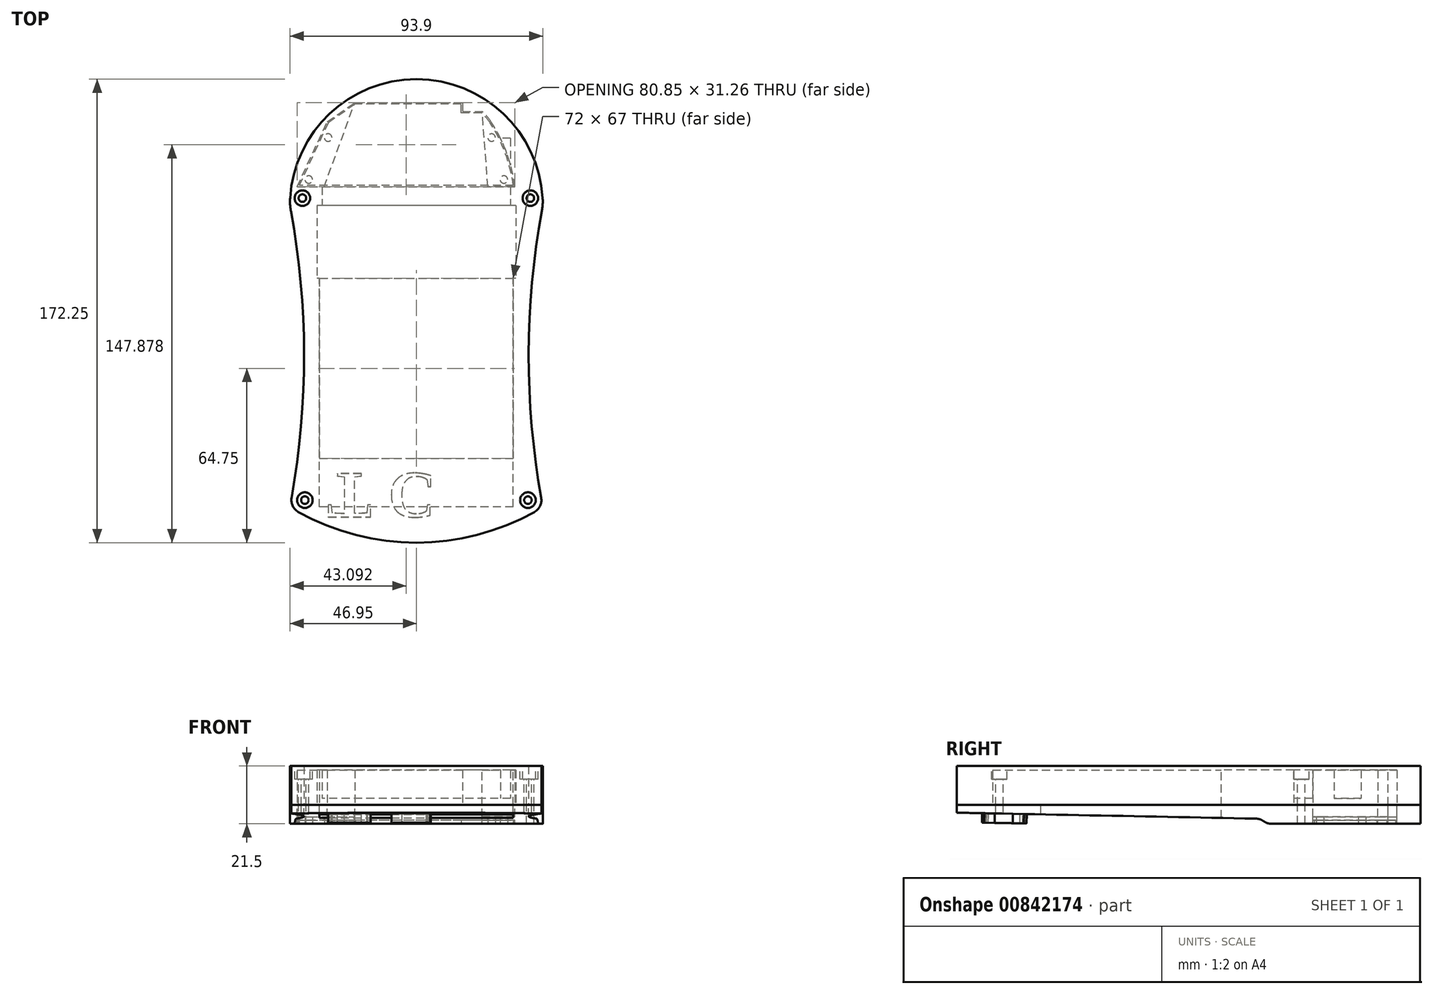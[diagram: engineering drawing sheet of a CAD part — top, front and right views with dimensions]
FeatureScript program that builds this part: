
annotation { "Feature Type Name" : "Feature", "Feature Type Description" : "" }
export const myFeature = defineFeature(function(context is Context, id is Id, definition is map)
    precondition{}
    {
        {
            var Q0;
            Q0=qCreatedBy(makeId("Top.planeOp"),FACE);
            var sketch = newSketch(context, id + "F0", { "sketchPlane" : qUnion([Q0])});
            skLineSegment(sketch, "E0.bottom", {"start": v(36, -56) * mm, "end": v(-36, -56) * mm});
            skLineSegment(sketch, "E0.top", {"start": v(36, 56) * mm, "end": v(-36, 56) * mm});
            skLineSegment(sketch, "E0.left", {"start": v(36, -56) * mm, "end": v(36, 56) * mm});
            skLineSegment(sketch, "E0.right", {"start": v(-36, -56) * mm, "end": v(-36, 56) * mm});
            skPoint(sketch, "E0.middle", {"position": v(0, 0) * mm});
            skArc(sketch, "E1", {"start": v(47, 56) * mm, "mid": v(0, 103) * mm, "end": v(-47, 56) * mm});
            skArc(sketch, "E2", {"start": v(-47, -56) * mm, "mid": v(-41.73, 0) * mm, "end": v(-47, 56) * mm});
            skLineSegment(sketch, "E3", {"start": v(0, 117.63) * mm, "end": v(0, -101.58) * mm, "construction": true});
            skLineSegment(sketch, "E4", {"start": v(-114.42, 0) * mm, "end": v(113.04, 0) * mm, "construction": true});
            skArc(sketch, "E5.MirrorCS", {"start": v(47, -56) * mm, "mid": v(0, -103) * mm, "end": v(-47, -56) * mm});
            skArc(sketch, "E6.MirrorCS", {"start": v(47, -56) * mm, "mid": v(41.73, 0) * mm, "end": v(47, 56) * mm});
            skSolve(sketch);
        }
        {
            var Q0;
            Q0=makeQuery(id+"F0.imprint","IMPRINT",FACE,{"disambiguationData":[TD([[makeQuery(id+"F0.imprint","IMPRINT",EDGE,{"derivedFrom":sQuery(id+"F0.wireOp",EDGE,"E0.bottom")}),1.0]])]});
            extrude(context, id + "F1", {"entities" : qUnion([Q0]), "depth" : 14.5 * mm, "offsetDistance" : 25 * mm});
        }
        {
            var Q0;
            Q0=makeQuery(id+"F1.opExtrude","CAP_FACE",FACE,{"disambiguationData":[OSD([sQuery(id+"F0.wireOp",EDGE,"E0.bottom"),sQuery(id+"F0.wireOp",EDGE,"E0.top"),sQuery(id+"F0.wireOp",EDGE,"E0.left"),sQuery(id+"F0.wireOp",EDGE,"E0.right"),sQuery(id+"F0.wireOp",EDGE,"E1"),sQuery(id+"F0.wireOp",EDGE,"E2"),sQuery(id+"F0.wireOp",EDGE,"E5.MirrorCS"),sQuery(id+"F0.wireOp",EDGE,"E6.MirrorCS")])],"isStart":false});
            var sketch = newSketch(context, id + "F2", { "sketchPlane" : qUnion([Q0])});
            skLineSegment(sketch, "E7.bottom", {"start": v(36, -56) * mm, "end": v(-36, -56) * mm});
            skLineSegment(sketch, "E7.top", {"start": v(36, 56) * mm, "end": v(-36, 56) * mm});
            skLineSegment(sketch, "E7.left", {"start": v(36, -56) * mm, "end": v(36, 56) * mm});
            skLineSegment(sketch, "E7.right", {"start": v(-36, -56) * mm, "end": v(-36, 56) * mm});
            skPoint(sketch, "E7.middle", {"position": v(0, 0) * mm});
            skSolve(sketch);
        }
        {
            var Q0;
            Q0=qSketchRegion(id+"F2",true);
            extrude(context, id + "F3", {"entities" : qUnion([Q0]), "operationType" : NewBodyOperationType.ADD, "oppositeDirection" : true, "depth" : 1.5 * mm, "offsetDistance" : 25 * mm});
        }
        {
            var Q0;
            Q0=makeQuery(id+"F1.opExtrude","CAP_FACE",FACE,{"disambiguationData":[OSD([sQuery(id+"F0.wireOp",EDGE,"E0.bottom"),sQuery(id+"F0.wireOp",EDGE,"E0.top"),sQuery(id+"F0.wireOp",EDGE,"E0.left"),sQuery(id+"F0.wireOp",EDGE,"E0.right"),sQuery(id+"F0.wireOp",EDGE,"E1"),sQuery(id+"F0.wireOp",EDGE,"E2"),sQuery(id+"F0.wireOp",EDGE,"E5.MirrorCS"),sQuery(id+"F0.wireOp",EDGE,"E6.MirrorCS")])],"isStart":true});
            var sketch = newSketch(context, id + "F4", { "sketchPlane" : qUnion([Q0])});
            skLineSegment(sketch, "E8", {"start": v(0, -56) * mm, "end": v(0, -29) * mm, "construction": true});
            skLineSegment(sketch, "E9.bottom", {"start": v(37, -56) * mm, "end": v(-37, -56) * mm});
            skLineSegment(sketch, "E9.top", {"start": v(37, -29) * mm, "end": v(-37, -29) * mm});
            skLineSegment(sketch, "E9.left", {"start": v(37, -56) * mm, "end": v(37, -29) * mm});
            skLineSegment(sketch, "E9.right", {"start": v(-37, -56) * mm, "end": v(-37, -29) * mm});
            skPoint(sketch, "E9.middle", {"position": v(0, -42.5) * mm});
            skSolve(sketch);
        }
        {
            var Q0;
            Q0=qSketchRegion(id+"F4",true);
            var Q1;
            Q1=makeQuery(id+"F3.opExtrude","CAP_FACE",FACE,{"disambiguationData":[OSD([sQuery(id+"F2.wireOp",EDGE,"E7.bottom"),sQuery(id+"F2.wireOp",EDGE,"E7.top"),sQuery(id+"F2.wireOp",EDGE,"E7.left"),sQuery(id+"F2.wireOp",EDGE,"E7.right")])],"isStart":false});
            extrude(context, id + "F5", {"entities" : qUnion([Q0]), "operationType" : NewBodyOperationType.REMOVE, "endBound" : BoundingType.UP_TO_SURFACE, "oppositeDirection" : true, "depth" : 25 * mm, "endBoundEntityFace" : qUnion([Q1]), "offsetDistance" : 25 * mm});
        }
        {
            var Q0;
            Q0=makeQuery(id+"F1.opExtrude","CAP_FACE",FACE,{"disambiguationData":[OSD([sQuery(id+"F0.wireOp",EDGE,"E0.bottom"),sQuery(id+"F0.wireOp",EDGE,"E0.top"),sQuery(id+"F0.wireOp",EDGE,"E0.left"),sQuery(id+"F0.wireOp",EDGE,"E0.right"),sQuery(id+"F0.wireOp",EDGE,"E1"),sQuery(id+"F0.wireOp",EDGE,"E2"),sQuery(id+"F0.wireOp",EDGE,"E5.MirrorCS"),sQuery(id+"F0.wireOp",EDGE,"E6.MirrorCS")])],"isStart":true});
            var sketch = newSketch(context, id + "F6", { "sketchPlane" : qUnion([Q0])});
            skArc(sketch, "E10", {"start": v(47, 56) * mm, "mid": v(0, 69.25) * mm, "end": v(-47, 56) * mm});
            skArc(sketch, "E11.0", {"start": v(47, 56) * mm, "mid": v(0, 103) * mm, "end": v(-47, 56) * mm});
            skSolve(sketch);
        }
        {
            var Q0;
            Q0=qSketchRegion(id+"F6",true);
            extrude(context, id + "F7", {"entities" : qUnion([Q0]), "operationType" : NewBodyOperationType.REMOVE, "oppositeDirection" : true, "depth" : 25 * mm, "offsetDistance" : 25 * mm});
        }
        {
            var Q0;
            Q0=makeQuery(id+"F1.opExtrude","CAP_FACE",FACE,{"disambiguationData":[OSD([sQuery(id+"F0.wireOp",EDGE,"E0.bottom"),sQuery(id+"F0.wireOp",EDGE,"E0.top"),sQuery(id+"F0.wireOp",EDGE,"E0.left"),sQuery(id+"F0.wireOp",EDGE,"E0.right"),sQuery(id+"F0.wireOp",EDGE,"E1"),sQuery(id+"F0.wireOp",EDGE,"E2"),sQuery(id+"F0.wireOp",EDGE,"E5.MirrorCS"),sQuery(id+"F0.wireOp",EDGE,"E6.MirrorCS")])],"isStart":true});
            var sketch = newSketch(context, id + "F8", { "sketchPlane" : qUnion([Q0])});
            skArc(sketch, "E12", {"start": v(27.76, -87.12) * mm, "mid": v(33.54, -75.56) * mm, "end": v(36.57, -63) * mm});
            skLineSegment(sketch, "E13", {"start": v(0, 109.51) * mm, "end": v(0, -146.95) * mm, "construction": true});
            skArc(sketch, "E14.MirrorCS", {"start": v(-27.76, -87.12) * mm, "mid": v(-33.54, -75.56) * mm, "end": v(-36.57, -63) * mm});
            skLineSegment(sketch, "E15", {"start": v(-36.57, -63) * mm, "end": v(36.57, -63) * mm});
            skPoint(sketch, "E16.orphan", {"position": v(-47, -56) * mm});
            skPoint(sketch, "E17.orphan", {"position": v(47, -56) * mm});
            skPoint(sketch, "E18.orphan", {"position": v(37, -56) * mm});
            skPoint(sketch, "E19.orphan", {"position": v(-37, -56) * mm});
            skArc(sketch, "E20.0", {"start": v(20.57, -93.76) * mm, "mid": v(0, -99) * mm, "end": v(-20.57, -93.76) * mm});
            skPoint(sketch, "E21.orphan", {"position": v(-16, -100.2) * mm});
            skPoint(sketch, "E22.orphan", {"position": v(16, -100.2) * mm});
            skPoint(sketch, "E23.visualSharp", {"position": v(-25, -90.99) * mm});
            skArc(sketch, "E23.filletArc", {"start": v(-27.76, -87.12) * mm, "mid": v(-24.57, -90.89) * mm, "end": v(-20.57, -93.76) * mm});
            skPoint(sketch, "E24.visualSharp", {"position": v(25, -90.99) * mm});
            skArc(sketch, "E24.filletArc", {"start": v(20.57, -93.76) * mm, "mid": v(24.57, -90.89) * mm, "end": v(27.76, -87.12) * mm});
            skSolve(sketch);
        }
        {
            var Q0;
            Q0=qSketchRegion(id+"F8",true);
            extrude(context, id + "F9", {"entities" : qUnion([Q0]), "operationType" : NewBodyOperationType.REMOVE, "oppositeDirection" : true, "depth" : 13 * mm, "offsetDistance" : 25 * mm});
        }
        {
            var Q0;
            Q0=makeQuery(id+"F1.opExtrude","SWEPT_EDGE",EDGE,{"disambiguationData":[OSD([sQuery(id+"F0.wireOp",EDGE,"E1"),sQuery(id+"F0.wireOp",EDGE,"E2")])]});
            var Q1;
            Q1=makeQuery(id+"F1.opExtrude","SWEPT_EDGE",EDGE,{"disambiguationData":[OSD([sQuery(id+"F0.wireOp",EDGE,"E1"),sQuery(id+"F0.wireOp",EDGE,"E6.MirrorCS")])]});
            fillet(context, id + "F10", {"entities" : qUnion([Q0, Q1]), "radius" : 20 * mm, "tangentPropagation" : true, "allowEdgeOverflow" : false});
        }
        {
            var Q0;
            {var subQ0=sQuery(id+"F0.wireOp",EDGE,"E6.MirrorCS");Q0=makeQuery(id+"F7.boolean.opBoolean","MERGE",EDGE,{"derivedFrom":[makeQuery(id+"F1.opExtrude","SWEPT_EDGE",EDGE,{"disambiguationData":[OSD([sQuery(id+"F0.wireOp",EDGE,"E5.MirrorCS"),subQ0])]}),makeQuery(id+"F7.opExtrude","SWEPT_EDGE",EDGE,{"disambiguationData":[OSD([subQ0,sQuery(id+"F6.wireOp",EDGE,"E10"),sQuery(id+"F6.wireOp",EDGE,"E11.0")])]})]});}
            var Q1;
            {var subQ0=sQuery(id+"F0.wireOp",EDGE,"E2");Q1=makeQuery(id+"F7.boolean.opBoolean","MERGE",EDGE,{"derivedFrom":[makeQuery(id+"F1.opExtrude","SWEPT_EDGE",EDGE,{"disambiguationData":[OSD([subQ0,sQuery(id+"F0.wireOp",EDGE,"E5.MirrorCS")])]}),makeQuery(id+"F7.opExtrude","SWEPT_EDGE",EDGE,{"disambiguationData":[OSD([subQ0,sQuery(id+"F6.wireOp",EDGE,"E10"),sQuery(id+"F6.wireOp",EDGE,"E11.0")])]})]});}
            fillet(context, id + "F11", {"entities" : qUnion([Q0, Q1]), "radius" : 5 * mm, "tangentPropagation" : true, "allowEdgeOverflow" : false});
        }
        {
            var Q0;
            Q0=makeQuery(id+"F3.boolean.opBoolean","MERGE",FACE,{"derivedFrom":[makeQuery(id+"F1.opExtrude","CAP_FACE",FACE,{"disambiguationData":[OSD([sQuery(id+"F0.wireOp",EDGE,"E0.bottom"),sQuery(id+"F0.wireOp",EDGE,"E0.top"),sQuery(id+"F0.wireOp",EDGE,"E0.left"),sQuery(id+"F0.wireOp",EDGE,"E0.right"),sQuery(id+"F0.wireOp",EDGE,"E1"),sQuery(id+"F0.wireOp",EDGE,"E2"),sQuery(id+"F0.wireOp",EDGE,"E5.MirrorCS"),sQuery(id+"F0.wireOp",EDGE,"E6.MirrorCS")])],"isStart":false}),makeQuery(id+"F3.opExtrude","CAP_FACE",FACE,{"disambiguationData":[OSD([sQuery(id+"F2.wireOp",EDGE,"E7.bottom"),sQuery(id+"F2.wireOp",EDGE,"E7.top"),sQuery(id+"F2.wireOp",EDGE,"E7.left"),sQuery(id+"F2.wireOp",EDGE,"E7.right")])],"isStart":true})]});
            var sketch = newSketch(context, id + "F12", { "sketchPlane" : qUnion([Q0])});
            skCircle(sketch, "E25", {"center": v(-42.35, 58.78) * mm, "radius": 2.9 * mm});
            skLineSegment(sketch, "E26", {"start": v(0, 101.03) * mm, "end": v(0, -86.28) * mm, "construction": true});
            skCircle(sketch, "E27.MirrorC", {"center": v(42.35, 58.78) * mm, "radius": 2.9 * mm});
            skCircle(sketch, "E28", {"center": v(-41.45, -53.46) * mm, "radius": 2.9 * mm});
            skCircle(sketch, "E29.MirrorC", {"center": v(41.45, -53.46) * mm, "radius": 2.9 * mm});
            skSolve(sketch);
        }
        {
            var Q0;
            Q0=qSketchRegion(id+"F12",true);
            extrude(context, id + "F13", {"entities" : qUnion([Q0]), "operationType" : NewBodyOperationType.REMOVE, "oppositeDirection" : true, "depth" : 5 * mm, "offsetDistance" : 25 * mm});
        }
        {
            var Q0;
            Q0=makeQuery(id+"F13.boolean.opBoolean","COPY",FACE,{"derivedFrom":makeQuery(id+"F13.opExtrude","CAP_FACE",FACE,{"disambiguationData":[OSD([sQuery(id+"F12.wireOp",EDGE,"E25")])],"isStart":false})});
            var sketch = newSketch(context, id + "F14", { "sketchPlane" : qUnion([Q0])});
            skCircle(sketch, "E30", {"center": v(-42.35, 58.78) * mm, "radius": 1.4 * mm});
            skLineSegment(sketch, "E31", {"start": v(0, 85.8) * mm, "end": v(0, -75.06) * mm, "construction": true});
            skCircle(sketch, "E32", {"center": v(-41.45, -53.46) * mm, "radius": 1.4 * mm});
            skCircle(sketch, "E33.MirrorC", {"center": v(42.35, 58.78) * mm, "radius": 1.4 * mm});
            skCircle(sketch, "E34.MirrorC", {"center": v(41.45, -53.46) * mm, "radius": 1.4 * mm});
            skSolve(sketch);
        }
        {
            var Q0;
            Q0=qSketchRegion(id+"F14",true);
            extrude(context, id + "F15", {"entities" : qUnion([Q0]), "operationType" : NewBodyOperationType.REMOVE, "oppositeDirection" : true, "depth" : 25 * mm, "offsetDistance" : 25 * mm});
        }
        {
            var Q0;
            Q0=makeQuery(id+"F5.boolean.opBoolean","MERGE",FACE,{"derivedFrom":[makeQuery(id+"F1.opExtrude","SWEPT_FACE",FACE,{"disambiguationData":[OSD([sQuery(id+"F0.wireOp",EDGE,"E0.top")])]}),makeQuery(id+"F5.opExtrude","SWEPT_FACE",FACE,{"disambiguationData":[OSD([sQuery(id+"F4.wireOp",EDGE,"E9.bottom")])]})]});
            var sketch = newSketch(context, id + "F16", { "sketchPlane" : qUnion([Q0])});
            skLineSegment(sketch, "E35.bottom", {"start": v(-35, 13) * mm, "end": v(35, 13) * mm});
            skLineSegment(sketch, "E35.left", {"start": v(-35, 13) * mm, "end": v(-35, 2.5) * mm});
            skLineSegment(sketch, "E35.right", {"start": v(35, 13) * mm, "end": v(35, 2.5) * mm});
            skPoint(sketch, "E35.middle", {"position": v(0, 6.5) * mm});
            skLineSegment(sketch, "E36", {"start": v(35, 2.5) * mm, "end": v(-35, 2.5) * mm});
            skPoint(sketch, "E37.orphan", {"position": v(35, 0) * mm});
            skPoint(sketch, "E38.orphan", {"position": v(-35, 0) * mm});
            skSolve(sketch);
        }
        {
            var Q0;
            Q0=qSketchRegion(id+"F16",true);
            extrude(context, id + "F17", {"entities" : qUnion([Q0]), "operationType" : NewBodyOperationType.REMOVE, "oppositeDirection" : true, "depth" : 25 * mm, "offsetDistance" : 25 * mm});
        }
        {
            var Q0;
            Q0=makeQuery(id+"F9.boolean.opBoolean","COPY",FACE,{"derivedFrom":makeQuery(id+"F9.opExtrude","CAP_FACE",FACE,{"disambiguationData":[OSD([sQuery(id+"F8.wireOp",EDGE,"E12"),sQuery(id+"F8.wireOp",EDGE,"E14.MirrorCS"),sQuery(id+"F8.wireOp",EDGE,"E15"),sQuery(id+"F8.wireOp",EDGE,"E20.0"),sQuery(id+"F8.wireOp",EDGE,"E23.filletArc"),sQuery(id+"F8.wireOp",EDGE,"E24.filletArc")])],"isStart":false})});
            var sketch = newSketch(context, id + "F18", { "sketchPlane" : qUnion([Q0])});
            skPoint(sketch, "E39", {"position": v(24.45, -91) * mm});
            skLineSegment(sketch, "E40", {"start": v(24.45, -91) * mm, "end": v(-24.45, -91) * mm});
            skArc(sketch, "E41.0", {"start": v(-24.45, -91) * mm, "mid": v(-22.6, -92.5) * mm, "end": v(-20.57, -93.76) * mm});
            skArc(sketch, "E42.0", {"start": v(20.57, -93.76) * mm, "mid": v(0, -99) * mm, "end": v(-20.57, -93.76) * mm});
            skArc(sketch, "E43.0", {"start": v(20.57, -93.76) * mm, "mid": v(22.6, -92.5) * mm, "end": v(24.45, -91) * mm});
            skPoint(sketch, "E44.orphan", {"position": v(-27.76, -87.12) * mm});
            skPoint(sketch, "E45.orphan", {"position": v(27.76, -87.12) * mm});
            skSolve(sketch);
        }
        {
            var Q0;
            Q0=qSketchRegion(id+"F18",true);
            var Q1;
            Q1=makeQuery(id+"F1.opExtrude","CAP_FACE",FACE,{"disambiguationData":[OSD([sQuery(id+"F0.wireOp",EDGE,"E0.bottom"),sQuery(id+"F0.wireOp",EDGE,"E0.top"),sQuery(id+"F0.wireOp",EDGE,"E0.left"),sQuery(id+"F0.wireOp",EDGE,"E0.right"),sQuery(id+"F0.wireOp",EDGE,"E1"),sQuery(id+"F0.wireOp",EDGE,"E2"),sQuery(id+"F0.wireOp",EDGE,"E5.MirrorCS"),sQuery(id+"F0.wireOp",EDGE,"E6.MirrorCS")])],"isStart":true});
            extrude(context, id + "F19", {"entities" : qUnion([Q0]), "operationType" : NewBodyOperationType.ADD, "endBound" : BoundingType.UP_TO_SURFACE, "depth" : 25 * mm, "endBoundEntityFace" : qUnion([Q1]), "offsetDistance" : 25 * mm});
        }
        {
            var Q0;
            {var subQ0=sQuery(id+"F0.wireOp",EDGE,"E6.MirrorCS");var subQ1=sQuery(id+"F0.wireOp",EDGE,"E5.MirrorCS");var subQ2=sQuery(id+"F0.wireOp",EDGE,"E2");var subQ3=sQuery(id+"F0.wireOp",EDGE,"E1");var subQ4=sQuery(id+"F0.wireOp",EDGE,"E0.right");var subQ5=sQuery(id+"F0.wireOp",EDGE,"E0.left");var subQ6=sQuery(id+"F0.wireOp",EDGE,"E0.top");var subQ7=sQuery(id+"F0.wireOp",EDGE,"E0.bottom");Q0=makeQuery(id+"F19.boolean.opBoolean","MERGE",FACE,{"derivedFrom":[makeQuery(id+"F1.opExtrude","CAP_FACE",FACE,{"disambiguationData":[OSD([subQ7,subQ6,subQ5,subQ4,subQ3,subQ2,subQ1,subQ0])],"isStart":true}),makeQuery(id+"F19.opExtrude","CAP_FACE",FACE,{"disambiguationData":[OSD([subQ7,subQ6,subQ5,subQ4,subQ3,subQ2,subQ1,subQ0])],"isStart":false})]});}
            var sketch = newSketch(context, id + "F20", { "sketchPlane" : qUnion([Q0])});
            skLineSegment(sketch, "E46", {"start": v(-40.9, -63) * mm, "end": v(-33.2, -87.12) * mm});
            skLineSegment(sketch, "E47", {"start": v(-22.9, -63) * mm, "end": v(-40.9, -63) * mm});
            skLineSegment(sketch, "E48", {"start": v(-33.2, -87.12) * mm, "end": v(-22.9, -94.26) * mm});
            skLineSegment(sketch, "E49", {"start": v(-22.9, -94.26) * mm, "end": v(17.1, -94.26) * mm});
            skLineSegment(sketch, "E50", {"start": v(17.1, -94.26) * mm, "end": v(17.1, -63) * mm});
            skLineSegment(sketch, "E51", {"start": v(17.1, -63) * mm, "end": v(-22.9, -63) * mm});
            skSolve(sketch);
        }
        {
            var Q0;
            Q0 = qSketchRegion(id + "F20", true);
            var Q1;
            {var subQ0=sQuery(id+"F2.wireOp",EDGE,"E7.right");var subQ1=sQuery(id+"F2.wireOp",EDGE,"E7.left");var subQ2=sQuery(id+"F2.wireOp",EDGE,"E7.top");var subQ3=sQuery(id+"F2.wireOp",EDGE,"E7.bottom");Q1=makeQuery(id+"F17.boolean.opBoolean","MERGE",FACE,{"derivedFrom":[makeQuery(id+"F5.boolean.opBoolean","MERGE",FACE,{"derivedFrom":[makeQuery(id+"F3.opExtrude","CAP_FACE",FACE,{"disambiguationData":[OSD([subQ3,subQ2,subQ1,subQ0])],"isStart":false}),makeQuery(id+"F5.opExtrude","CAP_FACE",FACE,{"disambiguationData":[OSD([subQ3,subQ2,subQ1,subQ0])],"isStart":false})]}),makeQuery(id+"F9.boolean.opBoolean","COPY",FACE,{"derivedFrom":makeQuery(id+"F9.opExtrude","CAP_FACE",FACE,{"disambiguationData":[OSD([sQuery(id+"F8.wireOp",EDGE,"E12"),sQuery(id+"F8.wireOp",EDGE,"E14.MirrorCS"),sQuery(id+"F8.wireOp",EDGE,"E15"),sQuery(id+"F8.wireOp",EDGE,"E20.0"),sQuery(id+"F8.wireOp",EDGE,"E23.filletArc"),sQuery(id+"F8.wireOp",EDGE,"E24.filletArc")])],"isStart":false})}),makeQuery(id+"F17.opExtrude","SWEPT_FACE",FACE,{"disambiguationData":[OSD([sQuery(id+"F16.wireOp",EDGE,"E35.bottom")])]})]});}
            extrude(context, id + "F21", {"entities" : qUnion([Q0]), "operationType" : NewBodyOperationType.REMOVE, "endBound" : BoundingType.UP_TO_SURFACE, "oppositeDirection" : true, "depth" : 25 * mm, "endBoundEntityFace" : qUnion([Q1]), "offsetDistance" : 25 * mm});
        }
        {
            var Q0;
            {var subQ0=sQuery(id+"F0.wireOp",EDGE,"E6.MirrorCS");var subQ1=sQuery(id+"F0.wireOp",EDGE,"E5.MirrorCS");var subQ2=sQuery(id+"F0.wireOp",EDGE,"E2");var subQ3=sQuery(id+"F0.wireOp",EDGE,"E1");var subQ4=sQuery(id+"F0.wireOp",EDGE,"E0.right");var subQ5=sQuery(id+"F0.wireOp",EDGE,"E0.left");var subQ6=sQuery(id+"F0.wireOp",EDGE,"E0.top");var subQ7=sQuery(id+"F0.wireOp",EDGE,"E0.bottom");Q0=makeQuery(id+"F19.boolean.opBoolean","MERGE",FACE,{"derivedFrom":[makeQuery(id+"F1.opExtrude","CAP_FACE",FACE,{"disambiguationData":[OSD([subQ7,subQ6,subQ5,subQ4,subQ3,subQ2,subQ1,subQ0])],"isStart":true}),makeQuery(id+"F19.opExtrude","CAP_FACE",FACE,{"disambiguationData":[OSD([subQ7,subQ6,subQ5,subQ4,subQ3,subQ2,subQ1,subQ0])],"isStart":false})]});}
            var sketch = newSketch(context, id + "F22", { "sketchPlane" : qUnion([Q0])});
            skLineSegment(sketch, "E52", {"start": v(-40.9, -63) * mm, "end": v(-44.28, -63) * mm});
            skLineSegment(sketch, "E53", {"start": v(-44.28, -63) * mm, "end": v(-33.2, -87.12) * mm});
            skLineSegment(sketch, "E54.0", {"start": v(-40.9, -63) * mm, "end": v(-33.2, -87.12) * mm});
            skSolve(sketch);
        }
        {
            var Q0;
            Q0 = qSketchRegion(id + "F22", true);
            var Q1;
            {var subQ0=sQuery(id+"F16.wireOp",EDGE,"E35.bottom");var subQ1=sQuery(id+"F8.wireOp",EDGE,"E24.filletArc");var subQ2=sQuery(id+"F8.wireOp",EDGE,"E23.filletArc");var subQ3=sQuery(id+"F8.wireOp",EDGE,"E20.0");var subQ4=sQuery(id+"F8.wireOp",EDGE,"E15");var subQ5=sQuery(id+"F8.wireOp",EDGE,"E14.MirrorCS");var subQ6=sQuery(id+"F8.wireOp",EDGE,"E12");var subQ7=sQuery(id+"F2.wireOp",EDGE,"E7.right");var subQ8=sQuery(id+"F2.wireOp",EDGE,"E7.left");var subQ9=sQuery(id+"F2.wireOp",EDGE,"E7.top");var subQ10=sQuery(id+"F2.wireOp",EDGE,"E7.bottom");Q1=makeQuery(id+"F21.boolean.opBoolean","MERGE",FACE,{"derivedFrom":[makeQuery(id+"F17.boolean.opBoolean","MERGE",FACE,{"derivedFrom":[makeQuery(id+"F5.boolean.opBoolean","MERGE",FACE,{"derivedFrom":[makeQuery(id+"F3.opExtrude","CAP_FACE",FACE,{"disambiguationData":[OSD([subQ10,subQ9,subQ8,subQ7])],"isStart":false}),makeQuery(id+"F5.opExtrude","CAP_FACE",FACE,{"disambiguationData":[OSD([subQ10,subQ9,subQ8,subQ7])],"isStart":false})]}),makeQuery(id+"F9.boolean.opBoolean","COPY",FACE,{"derivedFrom":makeQuery(id+"F9.opExtrude","CAP_FACE",FACE,{"disambiguationData":[OSD([subQ6,subQ5,subQ4,subQ3,subQ2,subQ1])],"isStart":false})}),makeQuery(id+"F17.opExtrude","SWEPT_FACE",FACE,{"disambiguationData":[OSD([subQ0])]})]}),makeQuery(id+"F21.opExtrude","CAP_FACE",FACE,{"disambiguationData":[OSD([subQ10,subQ9,subQ8,subQ7,subQ6,subQ5,subQ4,subQ3,subQ2,subQ1,subQ0])],"isStart":false})]});}
            extrude(context, id + "F23", {"entities" : qUnion([Q0]), "operationType" : NewBodyOperationType.REMOVE, "endBound" : BoundingType.UP_TO_SURFACE, "oppositeDirection" : true, "depth" : 25 * mm, "endBoundEntityFace" : qUnion([Q1]), "offsetDistance" : 25 * mm});
        }
        {
            var Q0;
            {var subQ0=sQuery(id+"F0.wireOp",EDGE,"E6.MirrorCS");var subQ1=sQuery(id+"F0.wireOp",EDGE,"E5.MirrorCS");var subQ2=sQuery(id+"F0.wireOp",EDGE,"E2");var subQ3=sQuery(id+"F0.wireOp",EDGE,"E1");var subQ4=sQuery(id+"F0.wireOp",EDGE,"E0.right");var subQ5=sQuery(id+"F0.wireOp",EDGE,"E0.left");var subQ6=sQuery(id+"F0.wireOp",EDGE,"E0.top");var subQ7=sQuery(id+"F0.wireOp",EDGE,"E0.bottom");Q0=makeQuery(id+"F19.boolean.opBoolean","MERGE",FACE,{"derivedFrom":[makeQuery(id+"F1.opExtrude","CAP_FACE",FACE,{"disambiguationData":[OSD([subQ7,subQ6,subQ5,subQ4,subQ3,subQ2,subQ1,subQ0])],"isStart":true}),makeQuery(id+"F19.opExtrude","CAP_FACE",FACE,{"disambiguationData":[OSD([subQ7,subQ6,subQ5,subQ4,subQ3,subQ2,subQ1,subQ0])],"isStart":false})]});}
            var sketch = newSketch(context, id + "F24", { "sketchPlane" : qUnion([Q0])});
            skArc(sketch, "E55.0", {"start": v(46.92, -58.78) * mm, "mid": v(0, -103) * mm, "end": v(-46.92, -58.78) * mm});
            skArc(sketch, "E55.1", {"start": v(46.37, 52.58) * mm, "mid": v(45.97, 55.6) * mm, "end": v(43.89, 57.82) * mm});
            skArc(sketch, "E55.2", {"start": v(43.89, 57.82) * mm, "mid": v(0, 69.25) * mm, "end": v(-43.89, 57.82) * mm});
            skArc(sketch, "E55.3", {"start": v(-46.37, 52.58) * mm, "mid": v(-41.73, -0.72) * mm, "end": v(-46.63, -54) * mm});
            skArc(sketch, "E55.4", {"start": v(46.37, 52.58) * mm, "mid": v(41.73, -0.72) * mm, "end": v(46.63, -54) * mm});
            skLineSegment(sketch, "E55.5", {"start": v(-33.2, -87.12) * mm, "end": v(-22.9, -94.26) * mm});
            skArc(sketch, "E56.0", {"start": v(-43.89, 57.82) * mm, "mid": v(-45.97, 55.6) * mm, "end": v(-46.37, 52.58) * mm});
            skCircle(sketch, "E57.0", {"center": v(41.45, 53.46) * mm, "radius": 1.4 * mm});
            skArc(sketch, "E58.0", {"start": v(46.92, -58.78) * mm, "mid": v(46.92, -56.38) * mm, "end": v(46.63, -54) * mm});
            skArc(sketch, "E59.0", {"start": v(-46.63, -54) * mm, "mid": v(-46.92, -56.38) * mm, "end": v(-46.92, -58.78) * mm});
            skCircle(sketch, "E60.0", {"center": v(-42.35, -58.78) * mm, "radius": 1.4 * mm});
            skCircle(sketch, "E61.0", {"center": v(42.35, -58.78) * mm, "radius": 1.4 * mm});
            skCircle(sketch, "E62.0", {"center": v(-41.45, 53.46) * mm, "radius": 1.4 * mm});
            skLineSegment(sketch, "E63.0", {"start": v(-22.9, -94.26) * mm, "end": v(17.1, -94.26) * mm});
            skLineSegment(sketch, "E64.0", {"start": v(17.1, -94.26) * mm, "end": v(17.1, -91) * mm});
            skLineSegment(sketch, "E65.0", {"start": v(17.1, -91) * mm, "end": v(24.45, -91) * mm});
            skArc(sketch, "E66.0", {"start": v(24.45, -91) * mm, "mid": v(26.23, -89.16) * mm, "end": v(27.76, -87.12) * mm});
            skArc(sketch, "E67.0", {"start": v(27.76, -87.12) * mm, "mid": v(33.54, -75.56) * mm, "end": v(36.57, -63) * mm});
            skLineSegment(sketch, "E68.0", {"start": v(-44.28, -63) * mm, "end": v(36.57, -63) * mm});
            skLineSegment(sketch, "E69.0", {"start": v(-44.28, -63) * mm, "end": v(-33.2, -87.12) * mm});
            skSolve(sketch);
        }
        {
            var Q0;
            Q0 = qSketchRegion(id + "F24", true);
            extrude(context, id + "F25", {"entities" : qUnion([Q0]), "depth" : 7 * mm, "offsetDistance" : 25 * mm});
        }
        {
            var Q0;
            Q0=qCreatedBy(makeId("Right.planeOp"),FACE);
            var sketch = newSketch(context, id + "F26", { "sketchPlane" : qUnion([Q0])});
            skLineSegment(sketch, "E70", {"start": v(-69.25, -2.86) * mm, "end": v(45.75, -5.15) * mm});
            skLineSegment(sketch, "E71", {"start": v(45.75, -5.15) * mm, "end": v(45.75, -7) * mm});
            skLineSegment(sketch, "E72", {"start": v(-69.25, -2.86) * mm, "end": v(-69.25, -7) * mm});
            skLineSegment(sketch, "E73", {"start": v(-69.25, -7) * mm, "end": v(45.75, -7) * mm});
            skSolve(sketch);
        }
        {
            var Q0;
            Q0 = qSketchRegion(id + "F26", true);
            extrude(context, id + "F27", {"entities" : qUnion([Q0]), "operationType" : NewBodyOperationType.REMOVE, "endBound" : BoundingType.SYMMETRIC, "oppositeDirection" : true, "depth" : 147.6 * mm, "offsetDistance" : 25 * mm});
        }
        {
            var Q0;
            Q0=makeQuery(id+"F27.boolean.opBoolean","COPY",EDGE,{"derivedFrom":makeQuery(id+"F27.opExtrude","SWEPT_EDGE",EDGE,{"disambiguationData":[OSD([sQuery(id+"F26.wireOp",EDGE,"E70"),sQuery(id+"F26.wireOp",EDGE,"E71")])]})});
            fillet(context, id + "F28", {"entities" : qUnion([Q0]), "radius" : 5 * mm, "tangentPropagation" : true, "allowEdgeOverflow" : false});
        }
        {
            var Q0;
            Q0=makeQuery(id+"F28.opFillet","BLEND_EDGE",EDGE,{"blendedFrom":[makeQuery(id+"F27.boolean.opBoolean","COPY",EDGE,{"derivedFrom":makeQuery(id+"F27.opExtrude","SWEPT_EDGE",EDGE,{"disambiguationData":[OSD([sQuery(id+"F26.wireOp",EDGE,"E70"),sQuery(id+"F26.wireOp",EDGE,"E71")])]})}),makeQuery(id+"F25.opExtrude","CAP_FACE",FACE,{"disambiguationData":[OSD([sQuery(id+"F24.wireOp",EDGE,"E55.0"),sQuery(id+"F24.wireOp",EDGE,"E55.1"),sQuery(id+"F24.wireOp",EDGE,"E55.2"),sQuery(id+"F24.wireOp",EDGE,"E55.3"),sQuery(id+"F24.wireOp",EDGE,"E55.4"),sQuery(id+"F24.wireOp",EDGE,"E55.5"),sQuery(id+"F24.wireOp",EDGE,"E56.0"),sQuery(id+"F24.wireOp",EDGE,"E57.0"),sQuery(id+"F24.wireOp",EDGE,"E58.0"),sQuery(id+"F24.wireOp",EDGE,"E59.0"),sQuery(id+"F24.wireOp",EDGE,"E60.0"),sQuery(id+"F24.wireOp",EDGE,"E61.0"),sQuery(id+"F24.wireOp",EDGE,"E62.0"),sQuery(id+"F24.wireOp",EDGE,"E63.0"),sQuery(id+"F24.wireOp",EDGE,"E64.0"),sQuery(id+"F24.wireOp",EDGE,"E65.0"),sQuery(id+"F24.wireOp",EDGE,"E66.0"),sQuery(id+"F24.wireOp",EDGE,"E67.0"),sQuery(id+"F24.wireOp",EDGE,"E68.0"),sQuery(id+"F24.wireOp",EDGE,"E69.0")])],"isStart":false})],"blendedInto":[makeQuery(id+"F25.opExtrude","CAP_FACE",FACE,{"disambiguationData":[OSD([sQuery(id+"F24.wireOp",EDGE,"E55.0"),sQuery(id+"F24.wireOp",EDGE,"E55.1"),sQuery(id+"F24.wireOp",EDGE,"E55.2"),sQuery(id+"F24.wireOp",EDGE,"E55.3"),sQuery(id+"F24.wireOp",EDGE,"E55.4"),sQuery(id+"F24.wireOp",EDGE,"E55.5"),sQuery(id+"F24.wireOp",EDGE,"E56.0"),sQuery(id+"F24.wireOp",EDGE,"E57.0"),sQuery(id+"F24.wireOp",EDGE,"E58.0"),sQuery(id+"F24.wireOp",EDGE,"E59.0"),sQuery(id+"F24.wireOp",EDGE,"E60.0"),sQuery(id+"F24.wireOp",EDGE,"E61.0"),sQuery(id+"F24.wireOp",EDGE,"E62.0"),sQuery(id+"F24.wireOp",EDGE,"E63.0"),sQuery(id+"F24.wireOp",EDGE,"E64.0"),sQuery(id+"F24.wireOp",EDGE,"E65.0"),sQuery(id+"F24.wireOp",EDGE,"E66.0"),sQuery(id+"F24.wireOp",EDGE,"E67.0"),sQuery(id+"F24.wireOp",EDGE,"E68.0"),sQuery(id+"F24.wireOp",EDGE,"E69.0")])],"isStart":false})]});
            fillet(context, id + "F29", {"entities" : qUnion([Q0]), "radius" : 5 * mm, "tangentPropagation" : true, "allowEdgeOverflow" : false});
        }
        {
            var Q0;
            Q0=makeQuery(id+"F25.opExtrude","CAP_FACE",FACE,{"disambiguationData":[OSD([sQuery(id+"F24.wireOp",EDGE,"E55.0"),sQuery(id+"F24.wireOp",EDGE,"E55.1"),sQuery(id+"F24.wireOp",EDGE,"E55.2"),sQuery(id+"F24.wireOp",EDGE,"E55.3"),sQuery(id+"F24.wireOp",EDGE,"E55.4"),sQuery(id+"F24.wireOp",EDGE,"E55.5"),sQuery(id+"F24.wireOp",EDGE,"E56.0"),sQuery(id+"F24.wireOp",EDGE,"E57.0"),sQuery(id+"F24.wireOp",EDGE,"E58.0"),sQuery(id+"F24.wireOp",EDGE,"E59.0"),sQuery(id+"F24.wireOp",EDGE,"E60.0"),sQuery(id+"F24.wireOp",EDGE,"E61.0"),sQuery(id+"F24.wireOp",EDGE,"E62.0"),sQuery(id+"F24.wireOp",EDGE,"E63.0"),sQuery(id+"F24.wireOp",EDGE,"E64.0"),sQuery(id+"F24.wireOp",EDGE,"E65.0"),sQuery(id+"F24.wireOp",EDGE,"E66.0"),sQuery(id+"F24.wireOp",EDGE,"E67.0"),sQuery(id+"F24.wireOp",EDGE,"E68.0"),sQuery(id+"F24.wireOp",EDGE,"E69.0")])],"isStart":false});
            cPlane(context, id + "F30", {"entities" : qUnion([Q0]), "cplaneType" : CPlaneType.OFFSET, "offset" : 2.6 * mm, "oppositeDirection" : true, "width" : 150 * mm, "height" : 150 * mm});
        }
        {
            var Q0;
            Q0=qCreatedBy(id+"F30.planeOp",FACE);
            var sketch = newSketch(context, id + "F31", { "sketchPlane" : qUnion([Q0])});
            skLineSegment(sketch, "E74.0", {"start": v(-44.28, -63) * mm, "end": v(-34.28, -84.76) * mm});
            skLineSegment(sketch, "E75", {"start": v(-44.28, -63) * mm, "end": v(-34.28, -63) * mm});
            skPoint(sketch, "E76.orphan", {"position": v(-33.2, -87.12) * mm});
            skLineSegment(sketch, "E77", {"start": v(0, 7.8) * mm, "end": v(0, -94.03) * mm, "construction": true});
            skArc(sketch, "E78.0", {"start": v(27.76, -87.12) * mm, "mid": v(33.54, -75.56) * mm, "end": v(36.57, -63) * mm});
            skLineSegment(sketch, "E79", {"start": v(36.57, -63) * mm, "end": v(26.57, -63) * mm});
            skArc(sketch, "E80.0", {"start": v(26.57, -88.75) * mm, "mid": v(27.18, -87.95) * mm, "end": v(27.76, -87.12) * mm});
            skPoint(sketch, "E81.orphan", {"position": v(24.45, -91) * mm});
            skLineSegment(sketch, "E82.0", {"start": v(-44.28, -63) * mm, "end": v(-33.2, -87.12) * mm});
            skLineSegment(sketch, "E83.0", {"start": v(-33.2, -87.12) * mm, "end": v(-22.9, -94.26) * mm});
            skArc(sketch, "E84.0", {"start": v(24.45, -91) * mm, "mid": v(26.23, -89.16) * mm, "end": v(27.76, -87.12) * mm});
            skLineSegment(sketch, "E85", {"start": v(-34.28, -63) * mm, "end": v(-22.9, -94.26) * mm});
            skLineSegment(sketch, "E86", {"start": v(26.57, -63) * mm, "end": v(24.45, -91) * mm});
            skSolve(sketch);
        }
        {
            var Q0;
            Q0 = qSketchRegion(id + "F31", true);
            extrude(context, id + "F32", {"entities" : qUnion([Q0]), "operationType" : NewBodyOperationType.ADD, "depth" : 1.3 * mm, "offsetDistance" : 25 * mm});
        }
        {
            var Q0;
            Q0=makeQuery(id+"F25.opExtrude","CAP_FACE",FACE,{"disambiguationData":[OSD([sQuery(id+"F24.wireOp",EDGE,"E55.0"),sQuery(id+"F24.wireOp",EDGE,"E55.1"),sQuery(id+"F24.wireOp",EDGE,"E55.2"),sQuery(id+"F24.wireOp",EDGE,"E55.3"),sQuery(id+"F24.wireOp",EDGE,"E55.4"),sQuery(id+"F24.wireOp",EDGE,"E55.5"),sQuery(id+"F24.wireOp",EDGE,"E56.0"),sQuery(id+"F24.wireOp",EDGE,"E57.0"),sQuery(id+"F24.wireOp",EDGE,"E58.0"),sQuery(id+"F24.wireOp",EDGE,"E59.0"),sQuery(id+"F24.wireOp",EDGE,"E60.0"),sQuery(id+"F24.wireOp",EDGE,"E61.0"),sQuery(id+"F24.wireOp",EDGE,"E62.0"),sQuery(id+"F24.wireOp",EDGE,"E63.0"),sQuery(id+"F24.wireOp",EDGE,"E64.0"),sQuery(id+"F24.wireOp",EDGE,"E65.0"),sQuery(id+"F24.wireOp",EDGE,"E66.0"),sQuery(id+"F24.wireOp",EDGE,"E67.0"),sQuery(id+"F24.wireOp",EDGE,"E68.0"),sQuery(id+"F24.wireOp",EDGE,"E69.0")])],"isStart":false});
            var sketch = newSketch(context, id + "F33", { "sketchPlane" : qUnion([Q0])});
            skLineSegment(sketch, "E87.0", {"start": v(-43.5, -63.5) * mm, "end": v(-32.8, -86.78) * mm});
            skLineSegment(sketch, "E87.1", {"start": v(-32.8, -86.78) * mm, "end": v(-22.74, -93.76) * mm});
            skLineSegment(sketch, "E87.2", {"start": v(-43.5, -63.5) * mm, "end": v(36, -63.5) * mm});
            skLineSegment(sketch, "E87.3", {"start": v(-22.74, -93.76) * mm, "end": v(16.6, -93.76) * mm});
            skArc(sketch, "E87.4", {"start": v(27.34, -86.84) * mm, "mid": v(32.97, -75.66) * mm, "end": v(36, -63.5) * mm});
            skArc(sketch, "E87.5", {"start": v(24.26, -90.5) * mm, "mid": v(25.9, -88.77) * mm, "end": v(27.34, -86.84) * mm});
            skLineSegment(sketch, "E87.6", {"start": v(16.6, -90.5) * mm, "end": v(24.26, -90.5) * mm});
            skLineSegment(sketch, "E87.7", {"start": v(16.6, -93.76) * mm, "end": v(16.6, -90.5) * mm});
            skSolve(sketch);
        }
        {
            var Q0;
            Q0 = qSketchRegion(id + "F33", true);
            var Q1;
            Q1=makeQuery(id+"F32.opExtrude","CAP_FACE",FACE,{"disambiguationData":[OSD([sQuery(id+"F31.wireOp",EDGE,"E74.0"),sQuery(id+"F31.wireOp",EDGE,"E75"),sQuery(id+"F31.wireOp",EDGE,"EqfmIO8x-eZOM-xre8-AD1a-nbBecVC82i3M")])],"isStart":false});
            extrude(context, id + "F34", {"entities" : qUnion([Q0]), "endBound" : BoundingType.UP_TO_SURFACE, "oppositeDirection" : true, "depth" : 25 * mm, "endBoundEntityFace" : qUnion([Q1]), "offsetDistance" : 25 * mm});
        }
        {
            var Q0;
            Q0=makeQuery(id+"F34.opExtrude","CAP_FACE",FACE,{"disambiguationData":[OSD([sQuery(id+"F33.wireOp",EDGE,"E87.0"),sQuery(id+"F33.wireOp",EDGE,"E87.1"),sQuery(id+"F33.wireOp",EDGE,"E87.2"),sQuery(id+"F33.wireOp",EDGE,"E87.3"),sQuery(id+"F33.wireOp",EDGE,"E87.4"),sQuery(id+"F33.wireOp",EDGE,"E87.5"),sQuery(id+"F33.wireOp",EDGE,"E87.6"),sQuery(id+"F33.wireOp",EDGE,"E87.7")])],"isStart":true});
            var sketch = newSketch(context, id + "F35", { "sketchPlane" : qUnion([Q0])});
            skCircle(sketch, "E88", {"center": v(32.5, -65.7) * mm, "radius": 1.4 * mm});
            skCircle(sketch, "E89", {"center": v(-40, -65.7) * mm, "radius": 1.4 * mm});
            skCircle(sketch, "E90", {"center": v(-32.8, -81.28) * mm, "radius": 1.4 * mm});
            skCircle(sketch, "E91", {"center": v(27.94, -81.28) * mm, "radius": 1.4 * mm});
            skSolve(sketch);
        }
        {
            var Q0;
            Q0 = qSketchRegion(id + "F35", true);
            extrude(context, id + "F36", {"entities" : qUnion([Q0]), "operationType" : NewBodyOperationType.REMOVE, "oppositeDirection" : true, "depth" : 5 * mm, "offsetDistance" : 25 * mm});
        }
        {
            var Q0;
            {var subQ0=sQuery(id+"F16.wireOp",EDGE,"E35.bottom");var subQ1=sQuery(id+"F8.wireOp",EDGE,"E24.filletArc");var subQ2=sQuery(id+"F8.wireOp",EDGE,"E23.filletArc");var subQ3=sQuery(id+"F8.wireOp",EDGE,"E20.0");var subQ4=sQuery(id+"F8.wireOp",EDGE,"E15");var subQ5=sQuery(id+"F8.wireOp",EDGE,"E14.MirrorCS");var subQ6=sQuery(id+"F8.wireOp",EDGE,"E12");var subQ7=sQuery(id+"F2.wireOp",EDGE,"E7.right");var subQ8=sQuery(id+"F2.wireOp",EDGE,"E7.left");var subQ9=sQuery(id+"F2.wireOp",EDGE,"E7.top");var subQ10=sQuery(id+"F2.wireOp",EDGE,"E7.bottom");Q0=makeQuery(id+"F23.boolean.opBoolean","MERGE",FACE,{"derivedFrom":[makeQuery(id+"F21.boolean.opBoolean","MERGE",FACE,{"derivedFrom":[makeQuery(id+"F17.boolean.opBoolean","MERGE",FACE,{"derivedFrom":[makeQuery(id+"F5.boolean.opBoolean","MERGE",FACE,{"derivedFrom":[makeQuery(id+"F3.opExtrude","CAP_FACE",FACE,{"disambiguationData":[OSD([subQ10,subQ9,subQ8,subQ7])],"isStart":false}),makeQuery(id+"F5.opExtrude","CAP_FACE",FACE,{"disambiguationData":[OSD([subQ10,subQ9,subQ8,subQ7])],"isStart":false})]}),makeQuery(id+"F9.boolean.opBoolean","COPY",FACE,{"derivedFrom":makeQuery(id+"F9.opExtrude","CAP_FACE",FACE,{"disambiguationData":[OSD([subQ6,subQ5,subQ4,subQ3,subQ2,subQ1])],"isStart":false})}),makeQuery(id+"F17.opExtrude","SWEPT_FACE",FACE,{"disambiguationData":[OSD([subQ0])]})]}),makeQuery(id+"F21.opExtrude","CAP_FACE",FACE,{"disambiguationData":[OSD([subQ10,subQ9,subQ8,subQ7,subQ6,subQ5,subQ4,subQ3,subQ2,subQ1,subQ0])],"isStart":false})]}),makeQuery(id+"F23.opExtrude","CAP_FACE",FACE,{"disambiguationData":[OSD([subQ10,subQ9,subQ8,subQ7,subQ6,subQ5,subQ4,subQ3,subQ2,subQ1,subQ0])],"isStart":false})]});}
            var sketch = newSketch(context, id + "F37", { "sketchPlane" : qUnion([Q0])});
            skLineSegment(sketch, "E92.bottom", {"start": v(36, -29) * mm, "end": v(-36, -29) * mm});
            skLineSegment(sketch, "E92.top", {"start": v(36, 38) * mm, "end": v(-36, 38) * mm});
            skLineSegment(sketch, "E92.left", {"start": v(36, -29) * mm, "end": v(36, 38) * mm});
            skLineSegment(sketch, "E92.right", {"start": v(-36, -29) * mm, "end": v(-36, 38) * mm});
            skSolve(sketch);
        }
        {
            var Q0;
            Q0 = qSketchRegion(id + "F37", true);
            extrude(context, id + "F38", {"entities" : qUnion([Q0]), "operationType" : NewBodyOperationType.REMOVE, "depth" : 25 * mm, "offsetDistance" : 25 * mm});
        }
        {
            var Q0;
            Q0=makeQuery(id+"F27.boolean.opBoolean","COPY",FACE,{"derivedFrom":makeQuery(id+"F27.opExtrude","SWEPT_FACE",FACE,{"disambiguationData":[OSD([sQuery(id+"F26.wireOp",EDGE,"E70")])]})});
            var sketch = newSketch(context, id + "F39", { "sketchPlane" : qUnion([Q0])});
            skText(sketch, "E93", { "text": "T C", "fontName": "Tinos-Bold.ttf"});
            const initialGuessF39  = {"E93": [-0.03308, 0.04347, 1, 0, 0.01772]};
            skSetInitialGuess(sketch, initialGuessF39);
            skSolve(sketch);
        }
        {
            var Q0;
            Q0 = qSketchRegion(id + "F39", true);
            extrude(context, id + "F40", {"entities" : qUnion([Q0]), "depth" : 3.5 * mm, "offsetDistance" : 25 * mm});
        }
    });
